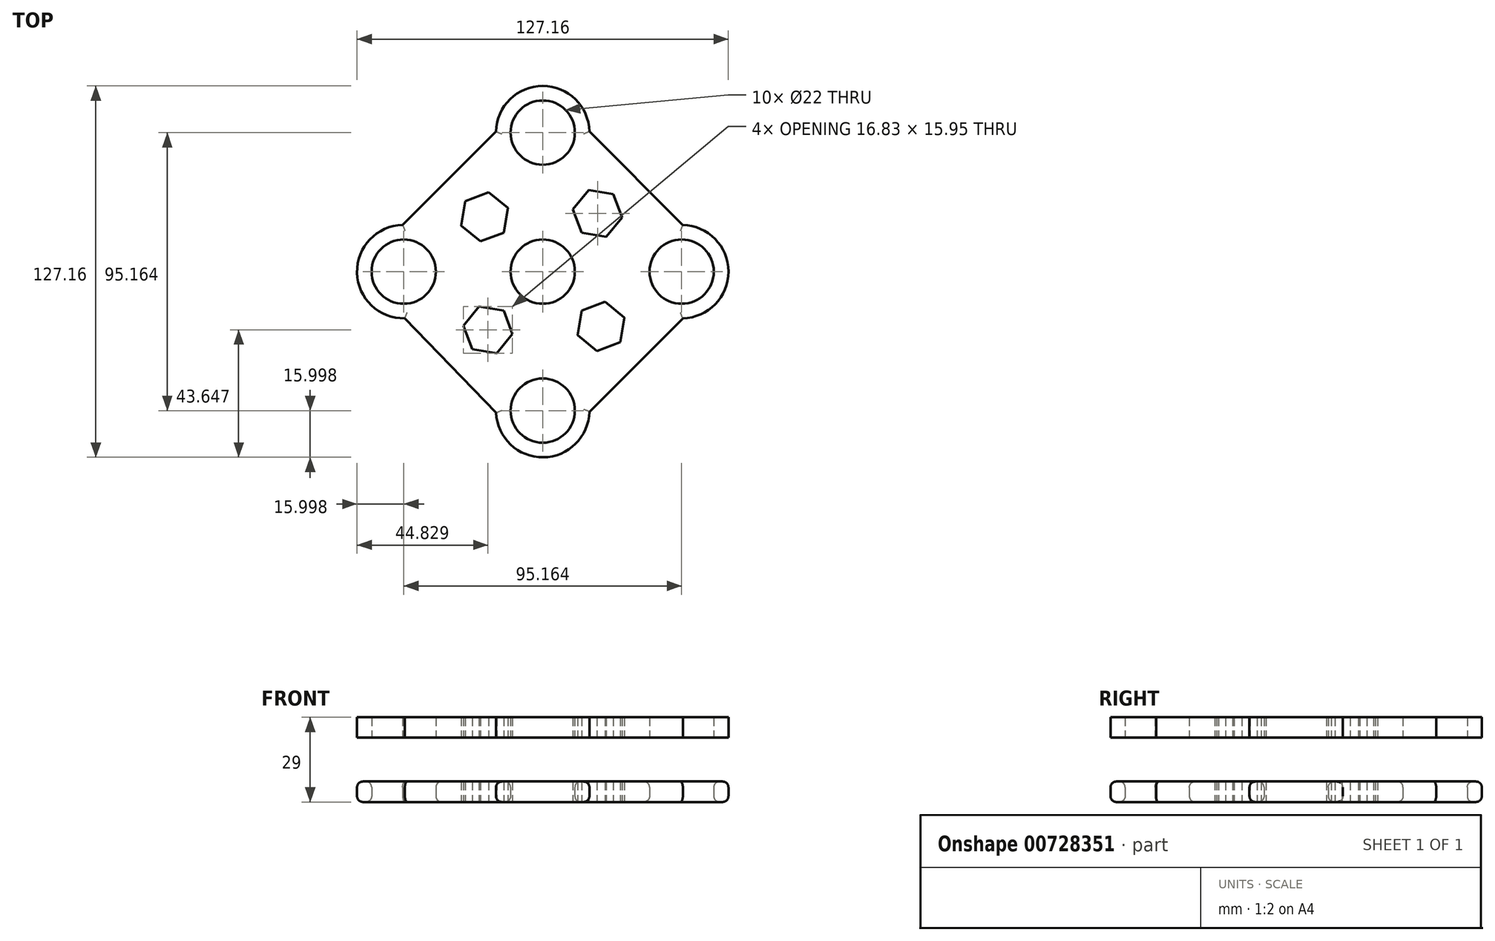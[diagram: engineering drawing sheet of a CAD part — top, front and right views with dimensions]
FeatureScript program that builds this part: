
annotation { "Feature Type Name" : "Feature", "Feature Type Description" : "" }
export const myFeature = defineFeature(function(context is Context, id is Id, definition is map)
    precondition{}
    {
        {
            var Q0;
            Q0=qCreatedBy(makeId("Top.planeOp"),FACE);
            var sketch = newSketch(context, id + "F0", { "sketchPlane" : qUnion([Q0])});
            skCircle(sketch, "E0", {"center": v(0, 0) * mm, "radius": 11 * mm});
            skCircle(sketch, "E1", {"center": v(0, 47.58) * mm, "radius": 11 * mm});
            skCircle(sketch, "E2.1.0", {"center": v(47.58, 0) * mm, "radius": 11 * mm});
            skCircle(sketch, "E2.2.0", {"center": v(0, -47.58) * mm, "radius": 11 * mm});
            skCircle(sketch, "E2.3.0", {"center": v(-47.58, 0) * mm, "radius": 11 * mm});
            skLineSegment(sketch, "E2.anchor1", {"start": v(0, 0) * mm, "end": v(0, 47.58) * mm, "construction": true});
            skLineSegment(sketch, "E2.anchor2", {"start": v(0, 0) * mm, "end": v(-47.58, 0) * mm, "construction": true});
            skArc(sketch, "E3", {"start": v(-47.97, 16) * mm, "mid": v(-63.58, -0.38) * mm, "end": v(-47.21, -16) * mm});
            skArc(sketch, "E4", {"start": v(16, 47.93) * mm, "mid": v(0, 63.58) * mm, "end": v(-16, 47.95) * mm});
            skArc(sketch, "E5", {"start": v(47.98, -16) * mm, "mid": v(63.58, 0.02) * mm, "end": v(47.95, 16) * mm});
            skArc(sketch, "E6", {"start": v(-15.98, -48.3) * mm, "mid": v(0.16, -63.58) * mm, "end": v(16, -47.98) * mm});
            skLineSegment(sketch, "E7", {"start": v(-16, 47.95) * mm, "end": v(-47.97, 16) * mm});
            skLineSegment(sketch, "E8", {"start": v(16, 47.93) * mm, "end": v(47.95, 16) * mm});
            skLineSegment(sketch, "E9", {"start": v(47.98, -16) * mm, "end": v(16, -47.98) * mm});
            skLineSegment(sketch, "E10", {"start": v(-15.98, -48.3) * mm, "end": v(-47.21, -16) * mm});
            skCircle(sketch, "E11.cCircle", {"center": v(-18.75, -19.93) * mm, "radius": 7.39 * mm, "construction": true});
            skLineSegment(sketch, "E11.0", {"start": v(-27.17, -18.56) * mm, "end": v(-21.77, -11.96) * mm});
            skLineSegment(sketch, "E11.1", {"start": v(-21.77, -11.96) * mm, "end": v(-13.35, -13.33) * mm});
            skLineSegment(sketch, "E11.2", {"start": v(-13.35, -13.33) * mm, "end": v(-10.33, -21.3) * mm});
            skLineSegment(sketch, "E11.3", {"start": v(-10.33, -21.3) * mm, "end": v(-15.73, -27.9) * mm});
            skLineSegment(sketch, "E11.4", {"start": v(-15.73, -27.9) * mm, "end": v(-24.15, -26.53) * mm});
            skLineSegment(sketch, "E11.5", {"start": v(-24.15, -26.53) * mm, "end": v(-27.17, -18.56) * mm});
            skPoint(sketch, "E11.0.midPoint", {"position": v(-24.47, -15.26) * mm});
            skLineSegment(sketch, "E12.1.0", {"start": v(26.53, -24.15) * mm, "end": v(18.56, -27.17) * mm});
            skLineSegment(sketch, "E12.1.1", {"start": v(27.9, -15.73) * mm, "end": v(26.53, -24.15) * mm});
            skLineSegment(sketch, "E12.1.2", {"start": v(21.3, -10.33) * mm, "end": v(27.9, -15.73) * mm});
            skLineSegment(sketch, "E12.1.3", {"start": v(13.33, -13.35) * mm, "end": v(21.3, -10.33) * mm});
            skLineSegment(sketch, "E12.1.4", {"start": v(11.96, -21.77) * mm, "end": v(13.33, -13.35) * mm});
            skLineSegment(sketch, "E12.1.5", {"start": v(18.56, -27.17) * mm, "end": v(11.96, -21.77) * mm});
            skLineSegment(sketch, "E12.2.0", {"start": v(24.15, 26.53) * mm, "end": v(27.17, 18.56) * mm});
            skLineSegment(sketch, "E12.2.1", {"start": v(15.73, 27.9) * mm, "end": v(24.15, 26.53) * mm});
            skLineSegment(sketch, "E12.2.2", {"start": v(10.33, 21.3) * mm, "end": v(15.73, 27.9) * mm});
            skLineSegment(sketch, "E12.2.3", {"start": v(13.35, 13.33) * mm, "end": v(10.33, 21.3) * mm});
            skLineSegment(sketch, "E12.2.4", {"start": v(21.77, 11.96) * mm, "end": v(13.35, 13.33) * mm});
            skLineSegment(sketch, "E12.2.5", {"start": v(27.17, 18.56) * mm, "end": v(21.77, 11.96) * mm});
            skLineSegment(sketch, "E12.3.0", {"start": v(-26.53, 24.15) * mm, "end": v(-18.56, 27.17) * mm});
            skLineSegment(sketch, "E12.3.1", {"start": v(-27.9, 15.73) * mm, "end": v(-26.53, 24.15) * mm});
            skLineSegment(sketch, "E12.3.2", {"start": v(-21.3, 10.33) * mm, "end": v(-27.9, 15.73) * mm});
            skLineSegment(sketch, "E12.3.3", {"start": v(-13.33, 13.35) * mm, "end": v(-21.3, 10.33) * mm});
            skLineSegment(sketch, "E12.3.4", {"start": v(-11.96, 21.77) * mm, "end": v(-13.33, 13.35) * mm});
            skLineSegment(sketch, "E12.3.5", {"start": v(-18.56, 27.17) * mm, "end": v(-11.96, 21.77) * mm});
            skSolve(sketch);
        }
        {
            var Q0;
            Q0 = qSketchRegion(id + "F0", true);
            extrude(context, id + "F1", {"entities" : qUnion([Q0]), "depth" : 7 * mm, "offsetDistance" : 25 * mm});
        }
        {
            var Q0;
            Q0=makeQuery(id+"F1.opExtrude","SWEPT_BODY",BODY,{"disambiguationData":[OSD([sQuery(id+"F0.wireOp",EDGE,"E0"),sQuery(id+"F0.wireOp",EDGE,"E1"),sQuery(id+"F0.wireOp",EDGE,"E2.1.0"),sQuery(id+"F0.wireOp",EDGE,"E2.2.0"),sQuery(id+"F0.wireOp",EDGE,"E2.3.0"),sQuery(id+"F0.wireOp",EDGE,"E3"),sQuery(id+"F0.wireOp",EDGE,"E4"),sQuery(id+"F0.wireOp",EDGE,"E5"),sQuery(id+"F0.wireOp",EDGE,"E6"),sQuery(id+"F0.wireOp",EDGE,"E7"),sQuery(id+"F0.wireOp",EDGE,"E8"),sQuery(id+"F0.wireOp",EDGE,"E9"),sQuery(id+"F0.wireOp",EDGE,"E10")])]});
            transform(context, id + "F2", {"entities" : qUnion([Q0]), "transformType" : TransformType.TRANSLATION_3D, "dx" : 0 * mm, "dy" : 0 * mm, "dz" : 22 * mm, "makeCopy" : true});
        }
        {
            var Q0;
            Q0=makeQuery(id+"F1.opExtrude","CAP_EDGE",EDGE,{"disambiguationData":[OSD([sQuery(id+"F0.wireOp",EDGE,"E7")])],"isStart":false});
            fillet(context, id + "F3", {"entities" : qUnion([Q0]), "radius" : 2 * mm, "tangentPropagation" : true, "allowEdgeOverflow" : false});
        }
        {
            var Q0;
            Q0=makeQuery(id+"F1.opExtrude","CAP_EDGE",EDGE,{"disambiguationData":[OSD([sQuery(id+"F0.wireOp",EDGE,"E4")])],"isStart":false});
            var Q1;
            Q1=makeQuery(id+"F1.opExtrude","CAP_EDGE",EDGE,{"disambiguationData":[OSD([sQuery(id+"F0.wireOp",EDGE,"E8")])],"isStart":false});
            var Q2;
            Q2=makeQuery(id+"F1.opExtrude","CAP_EDGE",EDGE,{"disambiguationData":[OSD([sQuery(id+"F0.wireOp",EDGE,"E5")])],"isStart":false});
            var Q3;
            Q3=makeQuery(id+"F1.opExtrude","CAP_EDGE",EDGE,{"disambiguationData":[OSD([sQuery(id+"F0.wireOp",EDGE,"E9")])],"isStart":false});
            var Q4;
            Q4=makeQuery(id+"F1.opExtrude","CAP_EDGE",EDGE,{"disambiguationData":[OSD([sQuery(id+"F0.wireOp",EDGE,"E6")])],"isStart":false});
            var Q5;
            Q5=makeQuery(id+"F1.opExtrude","CAP_EDGE",EDGE,{"disambiguationData":[OSD([sQuery(id+"F0.wireOp",EDGE,"E10")])],"isStart":false});
            var Q6;
            Q6=makeQuery(id+"F1.opExtrude","CAP_EDGE",EDGE,{"disambiguationData":[OSD([sQuery(id+"F0.wireOp",EDGE,"E3")])],"isStart":false});
            var Q7;
            Q7=makeQuery(id+"F1.opExtrude","CAP_EDGE",EDGE,{"disambiguationData":[OSD([sQuery(id+"F0.wireOp",EDGE,"E0")])],"isStart":false});
            var Q8;
            Q8=makeQuery(id+"F1.opExtrude","CAP_EDGE",EDGE,{"disambiguationData":[OSD([sQuery(id+"F0.wireOp",EDGE,"E7")])],"isStart":true});
            var Q9;
            Q9=makeQuery(id+"F1.opExtrude","CAP_EDGE",EDGE,{"disambiguationData":[OSD([sQuery(id+"F0.wireOp",EDGE,"E4")])],"isStart":true});
            var Q10;
            Q10=makeQuery(id+"F1.opExtrude","CAP_EDGE",EDGE,{"disambiguationData":[OSD([sQuery(id+"F0.wireOp",EDGE,"E8")])],"isStart":true});
            var Q11;
            Q11=makeQuery(id+"F1.opExtrude","CAP_EDGE",EDGE,{"disambiguationData":[OSD([sQuery(id+"F0.wireOp",EDGE,"E5")])],"isStart":true});
            var Q12;
            Q12=makeQuery(id+"F1.opExtrude","CAP_EDGE",EDGE,{"disambiguationData":[OSD([sQuery(id+"F0.wireOp",EDGE,"E9")])],"isStart":true});
            var Q13;
            Q13=makeQuery(id+"F1.opExtrude","CAP_EDGE",EDGE,{"disambiguationData":[OSD([sQuery(id+"F0.wireOp",EDGE,"E6")])],"isStart":true});
            var Q14;
            Q14=makeQuery(id+"F1.opExtrude","CAP_EDGE",EDGE,{"disambiguationData":[OSD([sQuery(id+"F0.wireOp",EDGE,"E10")])],"isStart":true});
            var Q15;
            Q15=makeQuery(id+"F1.opExtrude","CAP_EDGE",EDGE,{"disambiguationData":[OSD([sQuery(id+"F0.wireOp",EDGE,"E3")])],"isStart":true});
            var Q16;
            Q16=makeQuery(id+"F1.opExtrude","CAP_EDGE",EDGE,{"disambiguationData":[OSD([sQuery(id+"F0.wireOp",EDGE,"E0")])],"isStart":true});
            var Q17;
            Q17=makeQuery(id+"F1.opExtrude","CAP_EDGE",EDGE,{"disambiguationData":[OSD([sQuery(id+"F0.wireOp",EDGE,"E1")])],"isStart":false});
            var Q18;
            Q18=makeQuery(id+"F1.opExtrude","CAP_EDGE",EDGE,{"disambiguationData":[OSD([sQuery(id+"F0.wireOp",EDGE,"E2.1.0")])],"isStart":false});
            var Q19;
            Q19=makeQuery(id+"F1.opExtrude","CAP_EDGE",EDGE,{"disambiguationData":[OSD([sQuery(id+"F0.wireOp",EDGE,"E2.2.0")])],"isStart":false});
            var Q20;
            Q20=makeQuery(id+"F1.opExtrude","CAP_EDGE",EDGE,{"disambiguationData":[OSD([sQuery(id+"F0.wireOp",EDGE,"E2.3.0")])],"isStart":false});
            var Q21;
            Q21=makeQuery(id+"F1.opExtrude","CAP_EDGE",EDGE,{"disambiguationData":[OSD([sQuery(id+"F0.wireOp",EDGE,"E2.3.0")])],"isStart":true});
            var Q22;
            Q22=makeQuery(id+"F1.opExtrude","CAP_EDGE",EDGE,{"disambiguationData":[OSD([sQuery(id+"F0.wireOp",EDGE,"E1")])],"isStart":true});
            var Q23;
            Q23=makeQuery(id+"F1.opExtrude","CAP_EDGE",EDGE,{"disambiguationData":[OSD([sQuery(id+"F0.wireOp",EDGE,"E2.1.0")])],"isStart":true});
            var Q24;
            Q24=makeQuery(id+"F1.opExtrude","CAP_EDGE",EDGE,{"disambiguationData":[OSD([sQuery(id+"F0.wireOp",EDGE,"E2.2.0")])],"isStart":true});
            fillet(context, id + "F4", {"entities" : qUnion([Q0, Q1, Q2, Q3, Q4, Q5, Q6, Q7, Q8, Q9, Q10, Q11, Q12, Q13, Q14, Q15, Q16, Q17, Q18, Q19, Q20, Q21, Q22, Q23, Q24]), "radius" : 2 * mm, "tangentPropagation" : true, "allowEdgeOverflow" : false});
        }
    });
